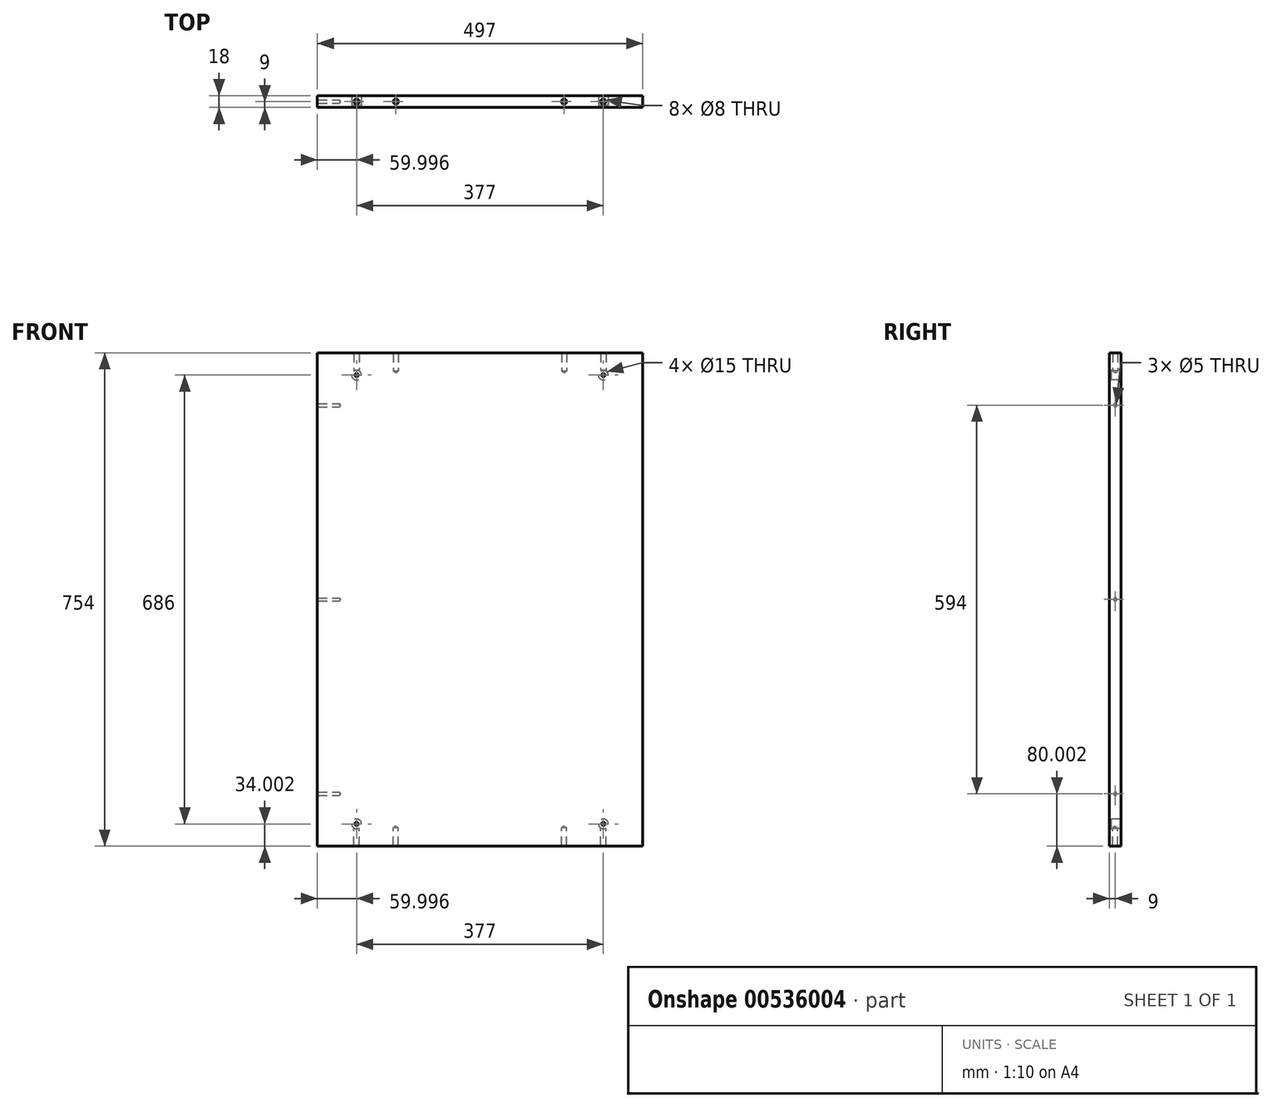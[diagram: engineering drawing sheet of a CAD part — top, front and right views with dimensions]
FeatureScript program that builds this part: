
annotation { "Feature Type Name" : "Feature", "Feature Type Description" : "" }
export const myFeature = defineFeature(function(context is Context, id is Id, definition is map)
    precondition{}
    {
        {
            var Q0;
            Q0=qCreatedBy(makeId("Front.planeOp"),FACE);
            cPlane(context, id + "F0", {"entities" : qUnion([Q0]), "cplaneType" : CPlaneType.OFFSET, "offset" : 283 * mm, "width" : 150 * mm, "height" : 150 * mm});
        }
        {
            var Q0;
            Q0=qCreatedBy(id+"F0.planeOp",FACE);
            var sketch = newSketch(context, id + "F1", { "sketchPlane" : qUnion([Q0])});
            skLineSegment(sketch, "E0.bottom", {"start": v(-247.2, 452.95) * mm, "end": v(249.8, 452.95) * mm});
            skLineSegment(sketch, "E0.top", {"start": v(-247.2, -301.05) * mm, "end": v(249.8, -301.05) * mm});
            skLineSegment(sketch, "E0.left", {"start": v(-247.2, 452.95) * mm, "end": v(-247.2, -301.05) * mm});
            skLineSegment(sketch, "E0.right", {"start": v(249.8, 452.95) * mm, "end": v(249.8, -301.05) * mm});
            skSolve(sketch);
        }
        {
            var Q0;
            Q0=makeQuery(id+"F1.imprint","IMPRINT",FACE,{"disambiguationData":[TD([[makeQuery(id+"F1.imprint","IMPRINT",EDGE,{"derivedFrom":sQuery(id+"F1.wireOp",EDGE,"E0.bottom")}),-1.0]])]});
            extrude(context, id + "F2", {"entities" : qUnion([Q0]), "depth" : 18 * mm, "offsetDistance" : 25 * mm});
        }
        {
            var Q0;
            Q0=makeQuery(id+"F2.opExtrude","SWEPT_FACE",FACE,{"disambiguationData":[OSD([sQuery(id+"F1.wireOp",EDGE,"E0.bottom")])]});
            var sketch = newSketch(context, id + "F3", { "sketchPlane" : qUnion([Q0])});
            skPoint(sketch, "E1", {"position": v(-187.2, -292) * mm});
            skPoint(sketch, "E1.positionSnap0", {"position": v(-247.2, -292) * mm});
            skPoint(sketch, "E2", {"position": v(-127.2, -292) * mm});
            skPoint(sketch, "E3", {"position": v(129.8, -292) * mm});
            skPoint(sketch, "E4", {"position": v(189.8, -292) * mm});
            skSolve(sketch);
        }
        {
            var Q0;
            Q0=makeQuery(id+"F2.opExtrude","SWEPT_FACE",FACE,{"disambiguationData":[OSD([sQuery(id+"F1.wireOp",EDGE,"E0.top")])]});
            var sketch = newSketch(context, id + "F4", { "sketchPlane" : qUnion([Q0])});
            skPoint(sketch, "E5", {"position": v(189.8, 292) * mm});
            skPoint(sketch, "E5.positionSnap0", {"position": v(249.8, 292) * mm});
            skPoint(sketch, "E6", {"position": v(129.8, 292) * mm});
            skPoint(sketch, "E7", {"position": v(-127.2, 292) * mm});
            skPoint(sketch, "E8", {"position": v(-187.2, 292) * mm});
            skSolve(sketch);
        }
        {
            var Q0;
            Q0=sQuery(id+"F3.wireOp",VERTEX,"E1");
            var Q1;
            Q1=sQuery(id+"F3.wireOp",VERTEX,"E2");
            var Q2;
            Q2=sQuery(id+"F3.wireOp",VERTEX,"E3");
            var Q3;
            Q3=sQuery(id+"F3.wireOp",VERTEX,"E4");
            var Q4;
            Q4=sQuery(id+"F4.wireOp",VERTEX,"E8");
            var Q5;
            Q5=sQuery(id+"F4.wireOp",VERTEX,"E7");
            var Q6;
            Q6=sQuery(id+"F4.wireOp",VERTEX,"E6");
            var Q7;
            Q7=sQuery(id+"F4.wireOp",VERTEX,"E5");
            var Q8;
            Q8=makeQuery(id+"F2.opExtrude","SWEPT_BODY",BODY,{"disambiguationData":[OSD([sQuery(id+"F1.wireOp",EDGE,"E0.bottom"),sQuery(id+"F1.wireOp",EDGE,"E0.top"),sQuery(id+"F1.wireOp",EDGE,"E0.left"),sQuery(id+"F1.wireOp",EDGE,"E0.right")])]});
            hole(context, id + "F5", {"style" : HoleStyle.SIMPLE, "endStyle" : HoleEndStyle.BLIND, "holeDiameter" : 8 * mm, "holeDepth" : 28 * mm, "isTappedThrough" : true, "tappedDepth" : 12 * mm, "tapClearance" : 3, "locations" : qUnion([Q0, Q1, Q2, Q3, Q4, Q5, Q6, Q7]), "scope" : qUnion([Q8])});
        }
        {
            var Q0;
            Q0=makeQuery(id+"F2.opExtrude","SWEPT_FACE",FACE,{"disambiguationData":[OSD([sQuery(id+"F1.wireOp",EDGE,"E0.left")])]});
            var sketch = newSketch(context, id + "F6", { "sketchPlane" : qUnion([Q0])});
            skPoint(sketch, "E9", {"position": v(292, 372.95) * mm});
            skPoint(sketch, "E9.positionSnap0", {"position": v(292, 452.95) * mm});
            skPoint(sketch, "E10", {"position": v(292, 75.95) * mm});
            skPoint(sketch, "E11", {"position": v(292, -221.05) * mm});
            skSolve(sketch);
        }
        {
            var Q0;
            Q0=sQuery(id+"F6.wireOp",VERTEX,"E9");
            var Q1;
            Q1=sQuery(id+"F6.wireOp",VERTEX,"E10");
            var Q2;
            Q2=sQuery(id+"F6.wireOp",VERTEX,"E11");
            var Q3;
            Q3=makeQuery(id+"F2.opExtrude","SWEPT_BODY",BODY,{"disambiguationData":[OSD([sQuery(id+"F1.wireOp",EDGE,"E0.bottom"),sQuery(id+"F1.wireOp",EDGE,"E0.top"),sQuery(id+"F1.wireOp",EDGE,"E0.left"),sQuery(id+"F1.wireOp",EDGE,"E0.right")])]});
            hole(context, id + "F7", {"style" : HoleStyle.SIMPLE, "endStyle" : HoleEndStyle.BLIND, "holeDiameter" : 5 * mm, "holeDepth" : 34 * mm, "isTappedThrough" : true, "tappedDepth" : 12 * mm, "tapClearance" : 3, "locations" : qUnion([Q0, Q1, Q2]), "scope" : qUnion([Q3])});
        }
        {
            var Q0;
            Q0=makeQuery(id+"F2.opExtrude","CAP_FACE",FACE,{"disambiguationData":[OSD([sQuery(id+"F1.wireOp",EDGE,"E0.bottom"),sQuery(id+"F1.wireOp",EDGE,"E0.top"),sQuery(id+"F1.wireOp",EDGE,"E0.left"),sQuery(id+"F1.wireOp",EDGE,"E0.right")])],"isStart":true});
            var sketch = newSketch(context, id + "F8", { "sketchPlane" : qUnion([Q0])});
            skPoint(sketch, "E12", {"position": v(-189.8, 418.95) * mm});
            skPoint(sketch, "E13", {"position": v(187.2, 418.95) * mm});
            skPoint(sketch, "E14", {"position": v(187.2, -267.05) * mm});
            skPoint(sketch, "E15", {"position": v(-189.8, -267.05) * mm});
            skSolve(sketch);
        }
        {
            var Q0;
            Q0=sQuery(id+"F8.wireOp",VERTEX,"E12");
            var Q1;
            Q1=sQuery(id+"F8.wireOp",VERTEX,"E13");
            var Q2;
            Q2=sQuery(id+"F8.wireOp",VERTEX,"E14");
            var Q3;
            Q3=sQuery(id+"F8.wireOp",VERTEX,"E15");
            var Q4;
            Q4=makeQuery(id+"F2.opExtrude","SWEPT_BODY",BODY,{"disambiguationData":[OSD([sQuery(id+"F1.wireOp",EDGE,"E0.bottom"),sQuery(id+"F1.wireOp",EDGE,"E0.top"),sQuery(id+"F1.wireOp",EDGE,"E0.left"),sQuery(id+"F1.wireOp",EDGE,"E0.right")])]});
            hole(context, id + "F9", {"style" : HoleStyle.SIMPLE, "endStyle" : HoleEndStyle.BLIND, "holeDiameter" : 15 * mm, "holeDepth" : 15 * mm, "isTappedThrough" : true, "tappedDepth" : 12 * mm, "tapClearance" : 3, "locations" : qUnion([Q0, Q1, Q2, Q3]), "scope" : qUnion([Q4])});
        }
    });
